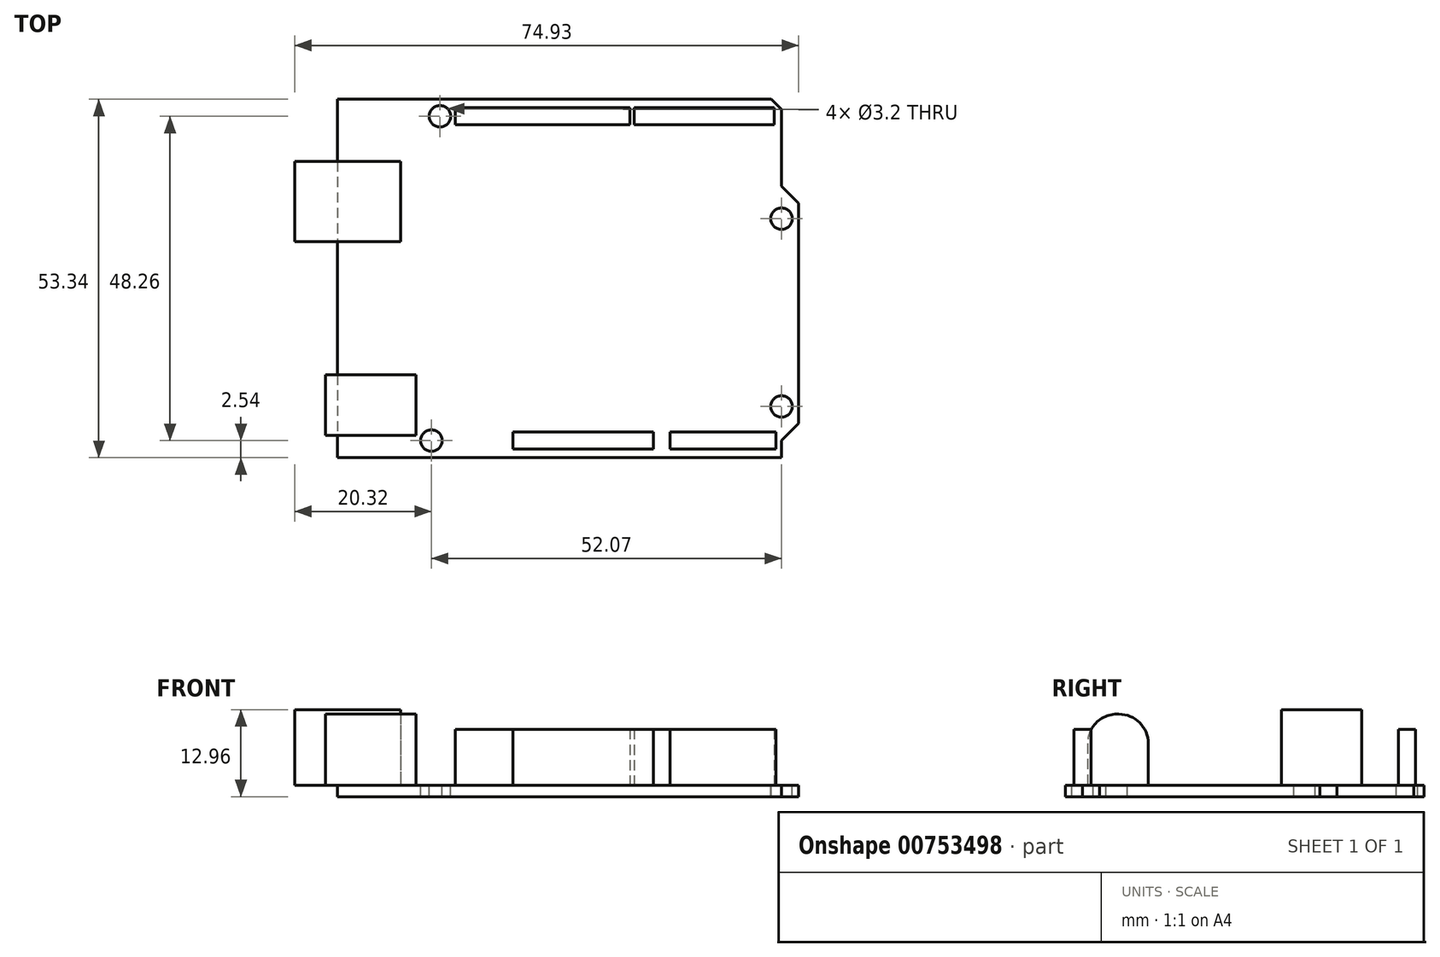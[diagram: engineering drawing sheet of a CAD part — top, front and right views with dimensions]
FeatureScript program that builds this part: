
annotation { "Feature Type Name" : "Feature", "Feature Type Description" : "" }
export const myFeature = defineFeature(function(context is Context, id is Id, definition is map)
    precondition{}
    {
        {
            var Q0;
            Q0=qCreatedBy(makeId("Top.planeOp"),FACE);
            var sketch = newSketch(context, id + "F0", { "sketchPlane" : qUnion([Q0])});
            skLineSegment(sketch, "E0", {"start": v(-34.3, 26.67) * mm, "end": v(-34.3, -26.67) * mm});
            skLineSegment(sketch, "E1", {"start": v(-34.3, -26.67) * mm, "end": v(31.75, -26.67) * mm});
            skLineSegment(sketch, "E2", {"start": v(31.75, -26.67) * mm, "end": v(31.75, -24.13) * mm});
            skLineSegment(sketch, "E3", {"start": v(31.75, -24.13) * mm, "end": v(34.3, -21.59) * mm});
            skLineSegment(sketch, "E4", {"start": v(34.3, -21.59) * mm, "end": v(34.3, 11.18) * mm});
            skLineSegment(sketch, "E5", {"start": v(34.3, 11.18) * mm, "end": v(31.75, 13.72) * mm});
            skLineSegment(sketch, "E6", {"start": v(31.75, 13.72) * mm, "end": v(31.75, 25.15) * mm});
            skLineSegment(sketch, "E7", {"start": v(30.23, 26.67) * mm, "end": v(-34.3, 26.67) * mm});
            skLineSegment(sketch, "E8", {"start": v(31.75, -19.05) * mm, "end": v(31.75, 8.9) * mm, "construction": true});
            skCircle(sketch, "E9", {"center": v(31.75, -19.05) * mm, "radius": 1.6 * mm});
            skCircle(sketch, "E10", {"center": v(31.75, 8.89) * mm, "radius": 1.6 * mm});
            skCircle(sketch, "E11", {"center": v(-19.05, 24.13) * mm, "radius": 1.6 * mm});
            skCircle(sketch, "E12", {"center": v(-20.32, -24.13) * mm, "radius": 1.6 * mm});
            skLineSegment(sketch, "E13", {"start": v(30.23, 26.67) * mm, "end": v(31.75, 25.15) * mm});
            skSolve(sketch);
        }
        {
            var Q0;
            Q0=qCreatedBy(makeId("Top.planeOp"),FACE);
            var sketch = newSketch(context, id + "F1", { "sketchPlane" : qUnion([Q0])});
            skLineSegment(sketch, "E14.bottom", {"start": v(-16.74, 25.4) * mm, "end": v(9.17, 25.4) * mm});
            skLineSegment(sketch, "E14.top", {"start": v(-16.74, 22.86) * mm, "end": v(9.17, 22.86) * mm});
            skLineSegment(sketch, "E14.left", {"start": v(-16.74, 25.4) * mm, "end": v(-16.74, 22.86) * mm});
            skLineSegment(sketch, "E14.right", {"start": v(9.17, 25.4) * mm, "end": v(9.17, 22.86) * mm});
            skLineSegment(sketch, "E15.bottom", {"start": v(9.83, 25.4) * mm, "end": v(30.66, 25.4) * mm});
            skLineSegment(sketch, "E15.top", {"start": v(9.83, 22.86) * mm, "end": v(30.66, 22.86) * mm});
            skLineSegment(sketch, "E15.left", {"start": v(9.83, 25.4) * mm, "end": v(9.83, 22.86) * mm});
            skLineSegment(sketch, "E15.right", {"start": v(30.66, 25.4) * mm, "end": v(30.66, 22.86) * mm});
            skLineSegment(sketch, "E16.bottom", {"start": v(-8.18, -22.86) * mm, "end": v(12.7, -22.86) * mm});
            skLineSegment(sketch, "E16.top", {"start": v(-8.18, -25.4) * mm, "end": v(12.7, -25.4) * mm});
            skLineSegment(sketch, "E16.left", {"start": v(-8.18, -22.86) * mm, "end": v(-8.18, -25.4) * mm});
            skLineSegment(sketch, "E16.right", {"start": v(12.7, -22.86) * mm, "end": v(12.7, -25.4) * mm});
            skLineSegment(sketch, "E17.bottom", {"start": v(15.14, -22.86) * mm, "end": v(30.89, -22.86) * mm});
            skLineSegment(sketch, "E17.top", {"start": v(15.14, -25.4) * mm, "end": v(30.89, -25.4) * mm});
            skLineSegment(sketch, "E17.left", {"start": v(15.14, -22.86) * mm, "end": v(15.14, -25.4) * mm});
            skLineSegment(sketch, "E17.right", {"start": v(30.89, -22.86) * mm, "end": v(30.89, -25.4) * mm});
            skLineSegment(sketch, "E18.bottom", {"start": v(-40.64, 17.4) * mm, "end": v(-24.9, 17.4) * mm});
            skLineSegment(sketch, "E18.top", {"start": v(-40.64, 5.46) * mm, "end": v(-24.9, 5.46) * mm});
            skLineSegment(sketch, "E18.left", {"start": v(-40.64, 17.4) * mm, "end": v(-40.64, 5.46) * mm});
            skLineSegment(sketch, "E18.right", {"start": v(-24.9, 17.4) * mm, "end": v(-24.9, 5.46) * mm});
            skLineSegment(sketch, "E19.bottom", {"start": v(-36.07, -14.35) * mm, "end": v(-22.61, -14.35) * mm});
            skLineSegment(sketch, "E19.top", {"start": v(-36.07, -23.37) * mm, "end": v(-22.61, -23.37) * mm});
            skLineSegment(sketch, "E19.left", {"start": v(-36.07, -14.35) * mm, "end": v(-36.07, -23.37) * mm});
            skLineSegment(sketch, "E19.right", {"start": v(-22.61, -14.35) * mm, "end": v(-22.61, -23.37) * mm});
            skLineSegment(sketch, "E20", {"start": v(15.14, -24.13) * mm, "end": v(30.89, -24.13) * mm, "construction": true});
            skLineSegment(sketch, "E21", {"start": v(9.83, 24.13) * mm, "end": v(30.66, 24.13) * mm, "construction": true});
            skSolve(sketch);
        }
        {
            var Q0;
            Q0=makeQuery(id+"F0.imprint","IMPRINT",FACE,{"disambiguationData":[TD([[makeQuery(id+"F0.imprint","IMPRINT",EDGE,{"derivedFrom":sQuery(id+"F0.wireOp",EDGE,"E0")}),1.0]])]});
            extrude(context, id + "F2", {"entities" : qUnion([Q0]), "oppositeDirection" : true, "depth" : 1.68 * mm, "offsetDistance" : 25.4 * mm});
        }
        {
            var Q0;
            Q0=makeQuery(id+"F1.imprint","IMPRINT",FACE,{"disambiguationData":[TD([[makeQuery(id+"F1.imprint","IMPRINT",EDGE,{"derivedFrom":sQuery(id+"F1.wireOp",EDGE,"E18.bottom")}),-1.0]])]});
            extrude(context, id + "F3", {"entities" : qUnion([Q0]), "operationType" : NewBodyOperationType.ADD, "depth" : 11.28 * mm, "offsetDistance" : 25.4 * mm});
        }
        {
            var Q0;
            Q0=makeQuery(id+"F1.imprint","IMPRINT",FACE,{"disambiguationData":[TD([[makeQuery(id+"F1.imprint","IMPRINT",EDGE,{"derivedFrom":sQuery(id+"F1.wireOp",EDGE,"E19.bottom")}),-1.0]])]});
            extrude(context, id + "F4", {"entities" : qUnion([Q0]), "operationType" : NewBodyOperationType.ADD, "depth" : 10.62 * mm, "offsetDistance" : 25.4 * mm});
        }
        {
            var Q0;
            Q0=makeQuery(id+"F4.opExtrude","CAP_EDGE",EDGE,{"disambiguationData":[OSD([sQuery(id+"F1.wireOp",EDGE,"E19.top")])],"isStart":false});
            var Q1;
            Q1=makeQuery(id+"F4.opExtrude","CAP_EDGE",EDGE,{"disambiguationData":[OSD([sQuery(id+"F1.wireOp",EDGE,"E19.bottom")])],"isStart":false});
            fillet(context, id + "F5", {"entities" : qUnion([Q0, Q1]), "radius" : 4.38 * mm, "tangentPropagation" : true, "allowEdgeOverflow" : false});
        }
        {
            var Q0;
            Q0=makeQuery(id+"F1.imprint","IMPRINT",FACE,{"disambiguationData":[TD([[makeQuery(id+"F1.imprint","IMPRINT",EDGE,{"derivedFrom":sQuery(id+"F1.wireOp",EDGE,"E16.bottom")}),-1.0]])]});
            var Q1;
            Q1=makeQuery(id+"F1.imprint","IMPRINT",FACE,{"disambiguationData":[TD([[makeQuery(id+"F1.imprint","IMPRINT",EDGE,{"derivedFrom":sQuery(id+"F1.wireOp",EDGE,"E17.bottom")}),-1.0]])]});
            var Q2;
            Q2=makeQuery(id+"F1.imprint","IMPRINT",FACE,{"disambiguationData":[TD([[makeQuery(id+"F1.imprint","IMPRINT",EDGE,{"derivedFrom":sQuery(id+"F1.wireOp",EDGE,"E14.bottom")}),-1.0]])]});
            var Q3;
            Q3=makeQuery(id+"F1.imprint","IMPRINT",FACE,{"disambiguationData":[TD([[makeQuery(id+"F1.imprint","IMPRINT",EDGE,{"derivedFrom":sQuery(id+"F1.wireOp",EDGE,"E15.bottom")}),-1.0]])]});
            extrude(context, id + "F6", {"entities" : qUnion([Q0, Q1, Q2, Q3]), "operationType" : NewBodyOperationType.ADD, "depth" : 8.36 * mm, "offsetDistance" : 25.4 * mm});
        }
    });
